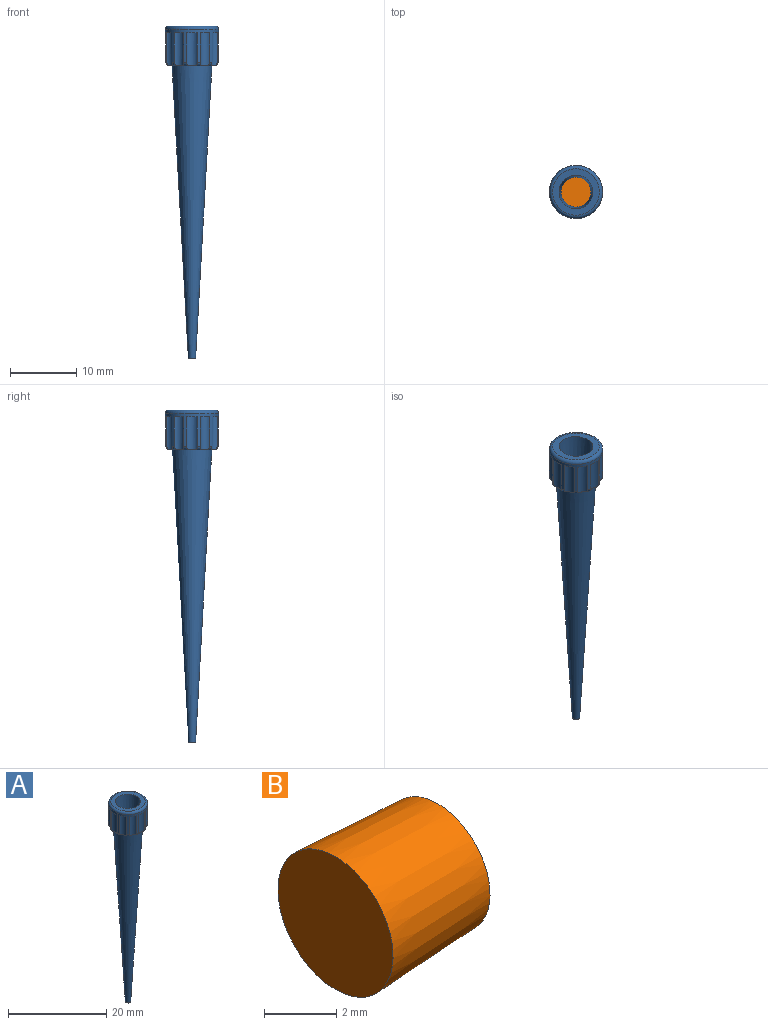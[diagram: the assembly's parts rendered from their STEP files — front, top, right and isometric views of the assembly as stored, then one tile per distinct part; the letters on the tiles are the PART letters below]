
ASSEMBLY  parts=2 mates=1
PART A: 45 faces, bbox 8.7x8.7x50 mm
  f0: torus R=3.5mm, axis (0,0,-1), area 0.6mm2, adj f18,f19,f41,f43
  f1: torus R=3.5mm, axis (0,0,-1), area 0.6mm2, adj f18,f19,f39,f43
  f2: torus R=3.5mm, axis (0,0,-1), area 0.6mm2, adj f18,f19,f23,f41
  f3: torus R=3.5mm, axis (0,0,-1), area 0.6mm2, adj f18,f19,f37,f39
  f4: torus R=3.5mm, axis (0,0,-1), area 0.6mm2, adj f18,f19,f35,f37
  f5: torus R=3.5mm, axis (0,0,-1), area 0.6mm2, adj f18,f19,f33,f35
  f6: torus R=3.5mm, axis (0,0,-1), area 0.6mm2, adj f18,f19,f29,f33
  f7: torus R=3.5mm, axis (0,0,-1), area 0.6mm2, adj f18,f19,f29,f31
  f8: torus R=3.5mm, axis (0,0,-1), area 0.6mm2, adj f18,f19,f21,f31
  f9: torus R=3.5mm, axis (0,0,-1), area 0.6mm2, adj f18,f19,f21,f27
  f10: torus R=3.5mm, axis (0,0,-1), area 0.6mm2, adj f18,f19,f25,f27
  f11: torus R=3.5mm, axis (0,0,-1), area 0.6mm2, adj f18,f19,f23,f25
  f12: cone r=3mm half-angle=3.2deg, axis (0,0,1), area 491.5mm2, adj f13,f19
  f13: plane 1.1x1.1mm, normal (0,0,-1), area 0.9mm2, adj f12,f14
  f14: cylinder r=0.07mm len=0.15mm, axis (0,0,1), area 0mm2, adj f13,f15
  f15: plane 0.5x0.5mm, normal (0,0,1), area 0.2mm2, adj f14,f16
  f16: cone r=0.25mm half-angle=2.6deg, axis (0,0,1), area 439.6mm2, adj f15,f17
  f17: plane 7x7mm, normal (0,0,1), area 18.1mm2, adj f16,f20
  f18: cylinder r=4mm len=8mm, axis (0,0,1), area 37.3mm2, adj f0,f1,f2,f3,f4,f5,f6,f7
  f19: plane 7x7mm, normal (0,0,-1), area 10.2mm2, adj f0,f1,f2,f3,f4,f5,f6,f7
  f20: torus R=3.5mm, axis (0,0,1), area 18.8mm2, adj f17,f18
  f21: cylinder r=1mm len=5mm, axis (0,0,-1), area 9.3mm2, adj f8,f9,f18,f22
  f22: plane 1.62x0.5mm, normal (0,0,-1), area 0.6mm2, adj f18,f21
  f23: cylinder r=1mm len=5mm, axis (0,0,-1), area 9.3mm2, adj f2,f11,f18,f24
  f24: plane 1.62x0.5mm, normal (0,0,-1), area 0.6mm2, adj f18,f23
  f25: cylinder r=1mm len=5mm, axis (0,0,-1), area 9.3mm2, adj f10,f11,f18,f26
  f26: plane 1.41x0.9mm, normal (0,0,-1), area 0.6mm2, adj f18,f25
  f27: cylinder r=1mm len=5mm, axis (0,0,-1), area 9.3mm2, adj f9,f10,f18,f28
  f28: plane 1.41x0.9mm, normal (0,0,-1), area 0.6mm2, adj f18,f27
  f29: cylinder r=1mm len=5mm, axis (0,0,-1), area 9.3mm2, adj f6,f7,f18,f30
  f30: plane 1.41x0.9mm, normal (0,0,-1), area 0.6mm2, adj f18,f29
  f31: cylinder r=1mm len=5mm, axis (0,0,-1), area 9.3mm2, adj f7,f8,f18,f32
  f32: plane 1.41x0.9mm, normal (0,0,-1), area 0.6mm2, adj f18,f31
  f33: cylinder r=1mm len=5mm, axis (0,0,-1), area 9.3mm2, adj f5,f6,f18,f34
  f34: plane 1.62x0.5mm, normal (0,0,-1), area 0.6mm2, adj f18,f33
  f35: cylinder r=1mm len=5mm, axis (0,0,-1), area 9.3mm2, adj f4,f5,f18,f36
  f36: plane 1.41x0.9mm, normal (0,0,-1), area 0.6mm2, adj f18,f35
  f37: cylinder r=1mm len=5mm, axis (0,0,-1), area 9.3mm2, adj f3,f4,f18,f38
  f38: plane 1.41x0.9mm, normal (0,0,-1), area 0.6mm2, adj f18,f37
  f39: cylinder r=1mm len=5mm, axis (0,0,-1), area 9.3mm2, adj f1,f3,f18,f40
  f40: plane 1.62x0.5mm, normal (0,0,-1), area 0.6mm2, adj f18,f39
  f41: cylinder r=1mm len=5mm, axis (0,0,-1), area 9.3mm2, adj f0,f2,f18,f42
  f42: plane 1.41x0.9mm, normal (0,0,-1), area 0.6mm2, adj f18,f41
  f43: cylinder r=1mm len=5mm, axis (0,0,-1), area 9.3mm2, adj f0,f1,f18,f44
  f44: plane 1.41x0.9mm, normal (0,0,-1), area 0.6mm2, adj f18,f43
PART B: 3 faces, bbox 4x4.5x4.5 mm
  f0: plane 4.5x4.5mm, normal (-1,0,0), area 15.9mm2, adj f2
  f1: plane 4.08x4.08mm, normal (1,0,0), area 13.1mm2, adj f2
  f2: cone r=2.25mm half-angle=3deg, axis (-1,0,0), area 54mm2, adj f0,f1
PLACE A at identity
PLACE B rot(axis=(0,1,0),90deg) t=(0,0,43.04)mm
MATE cylindrical A.f0 <-> B.f2  axis (0,0,1) through (0,0,50)mm
